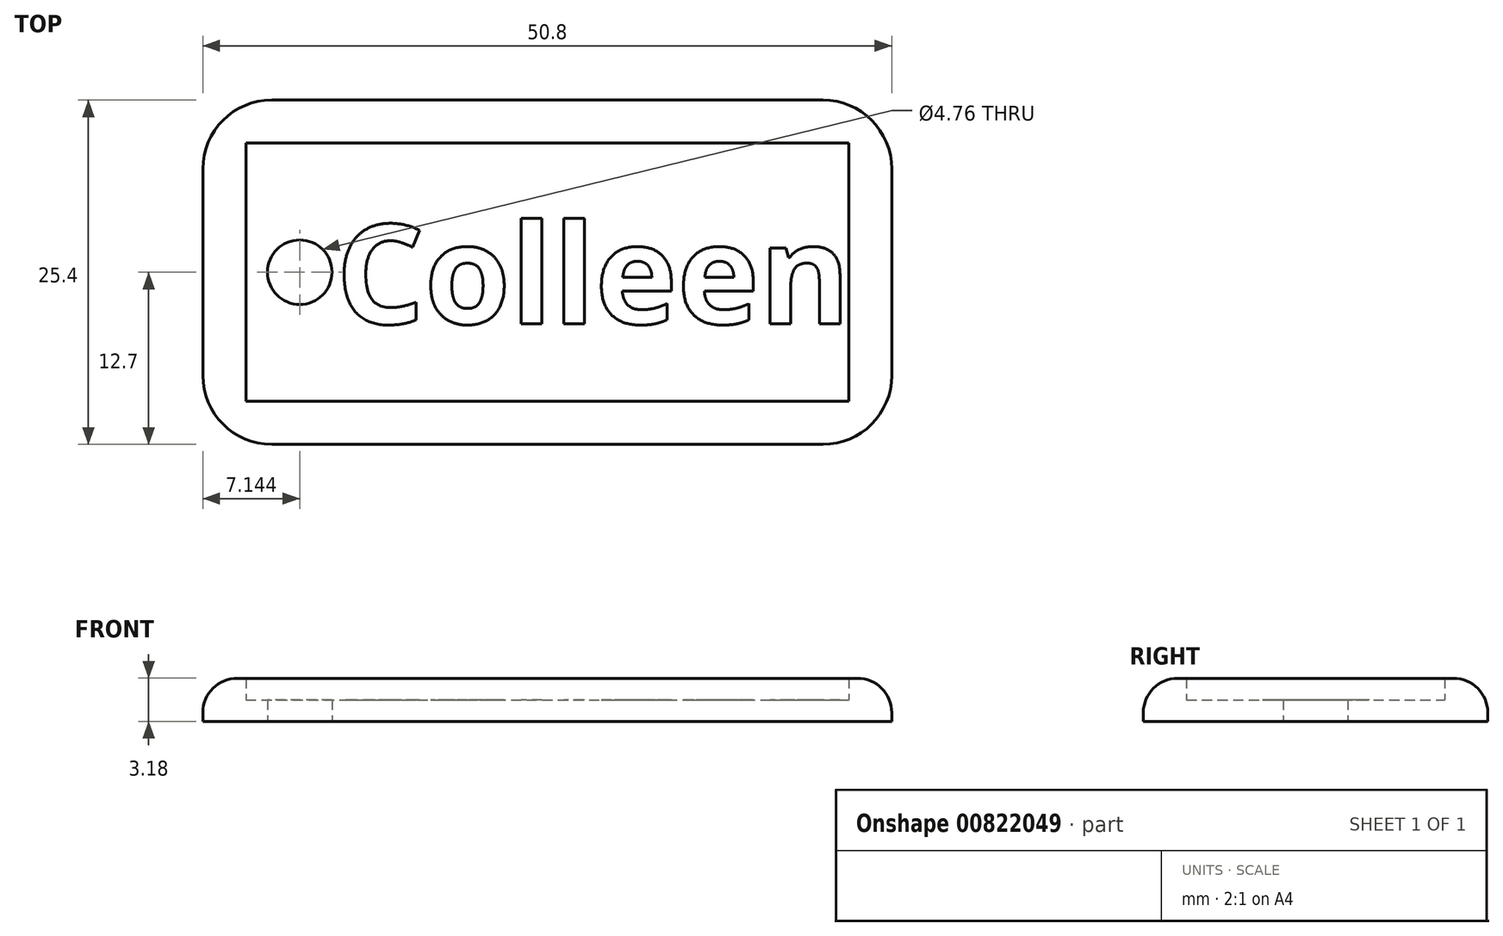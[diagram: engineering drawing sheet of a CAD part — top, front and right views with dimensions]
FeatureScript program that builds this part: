
annotation { "Feature Type Name" : "Feature", "Feature Type Description" : "" }
export const myFeature = defineFeature(function(context is Context, id is Id, definition is map)
    precondition{}
    {
        {
            var Q0;
            Q0=qCreatedBy(makeId("Top.planeOp"),FACE);
            var sketch = newSketch(context, id + "F0", { "sketchPlane" : qUnion([Q0])});
            skLineSegment(sketch, "E0.bottom", {"start": v(0, 0) * mm, "end": v(50.8, 0) * mm});
            skLineSegment(sketch, "E0.top", {"start": v(0, 25.4) * mm, "end": v(50.8, 25.4) * mm});
            skLineSegment(sketch, "E0.left", {"start": v(0, 0) * mm, "end": v(0, 25.4) * mm});
            skLineSegment(sketch, "E0.right", {"start": v(50.8, 0) * mm, "end": v(50.8, 25.4) * mm});
            skCircle(sketch, "E1", {"center": v(7.14, 12.7) * mm, "radius": 2.38 * mm});
            skPoint(sketch, "E1.centerSnap0", {"position": v(0, 12.7) * mm});
            skLineSegment(sketch, "E2.0", {"start": v(3.17, 22.23) * mm, "end": v(47.62, 22.23) * mm});
            skLineSegment(sketch, "E2.1", {"start": v(3.18, 3.18) * mm, "end": v(3.17, 22.22) * mm});
            skLineSegment(sketch, "E2.2", {"start": v(3.18, 3.18) * mm, "end": v(47.62, 3.18) * mm});
            skLineSegment(sketch, "E2.3", {"start": v(47.62, 3.18) * mm, "end": v(47.62, 22.23) * mm});
            skSolve(sketch);
        }
        {
            var Q0;
            Q0=makeQuery(id+"F0.imprint","IMPRINT",FACE,{"disambiguationData":[TD([[makeQuery(id+"F0.imprint","IMPRINT",EDGE,{"derivedFrom":sQuery(id+"F0.wireOp",EDGE,"E1")}),-1.0]])]});
            extrude(context, id + "F1", {"entities" : qUnion([Q0]), "depth" : 1.59 * mm, "offsetDistance" : 25.4 * mm});
        }
        {
            var Q0;
            Q0 = qSketchRegion(id + "F0", true);
            extrude(context, id + "F2", {"entities" : qUnion([Q0]), "operationType" : NewBodyOperationType.ADD, "depth" : 3.17 * mm, "offsetDistance" : 25.4 * mm});
        }
        {
            var Q0;
            Q0=makeQuery(id+"F2.opExtrude","SWEPT_EDGE",EDGE,{"disambiguationData":[OSD([sQuery(id+"F0.wireOp",EDGE,"E0.bottom"),sQuery(id+"F0.wireOp",EDGE,"E0.right")])]});
            var Q1;
            Q1=makeQuery(id+"F2.opExtrude","SWEPT_EDGE",EDGE,{"disambiguationData":[OSD([sQuery(id+"F0.wireOp",EDGE,"E0.top"),sQuery(id+"F0.wireOp",EDGE,"E0.right")])]});
            var Q2;
            Q2=makeQuery(id+"F2.opExtrude","SWEPT_EDGE",EDGE,{"disambiguationData":[OSD([sQuery(id+"F0.wireOp",EDGE,"E0.top"),sQuery(id+"F0.wireOp",EDGE,"E0.left")])]});
            var Q3;
            Q3=makeQuery(id+"F2.opExtrude","SWEPT_EDGE",EDGE,{"disambiguationData":[OSD([sQuery(id+"F0.wireOp",EDGE,"E0.bottom"),sQuery(id+"F0.wireOp",EDGE,"E0.left")])]});
            fillet(context, id + "F3", {"entities" : qUnion([Q0, Q1, Q2, Q3]), "radius" : 5.08 * mm, "tangentPropagation" : true, "allowEdgeOverflow" : false});
        }
        {
            var Q0;
            Q0=makeQuery(id+"F2.opExtrude","CAP_EDGE",EDGE,{"disambiguationData":[OSD([sQuery(id+"F0.wireOp",EDGE,"E0.top")])],"isStart":false});
            var Q1;
            Q1=makeQuery(id+"F2.opExtrude","CAP_EDGE",EDGE,{"disambiguationData":[OSD([sQuery(id+"F0.wireOp",EDGE,"E0.bottom")])],"isStart":false});
            fillet(context, id + "F4", {"entities" : qUnion([Q0, Q1]), "radius" : 2.54 * mm, "tangentPropagation" : true, "allowEdgeOverflow" : false});
        }
        {
            var Q0;
            Q0=makeQuery(id+"F1.opExtrude","CAP_FACE",FACE,{"disambiguationData":[OSD([sQuery(id+"F0.wireOp",EDGE,"E1"),sQuery(id+"F0.wireOp",EDGE,"E2.0"),sQuery(id+"F0.wireOp",EDGE,"E2.1"),sQuery(id+"F0.wireOp",EDGE,"E2.2"),sQuery(id+"F0.wireOp",EDGE,"E2.3")])],"isStart":false});
            var sketch = newSketch(context, id + "F5", { "sketchPlane" : qUnion([Q0])});
            skText(sketch, "E3", { "text": "Colleen", "fontName": "OpenSans-Bold.ttf"});
            const initialGuessF5  = {"E3": [0.00982, 0.0089, 1, 0, 0.00737]};
            skSetInitialGuess(sketch, initialGuessF5);
            skSolve(sketch);
        }
        {
            var Q0;
            Q0=makeQuery(id+"F5.imprint","IMPRINT",FACE,{"disambiguationData":[TD([[makeQuery(id+"F5.imprint","IMPRINT",EDGE,{"derivedFrom":sQuery(id+"F5.wireOp",EDGE,"E3.sketch_text.stroke-0")}),1.0]])]});
            var sketch = newSketch(context, id + "F6", { "sketchPlane" : qUnion([Q0])});
            skSolve(sketch);
        }
        {
            var Q0;
            Q0 = qSketchRegion(id + "F6", true);
            var Q1;
            Q1 = qSketchRegion(id + "F5", true);
            extrude(context, id + "F7", {"entities" : qUnion([Q0, Q1]), "operationType" : NewBodyOperationType.ADD, "depth" : 1 / 812.8 * mm, "offsetDistance" : 25.4 * mm});
        }
    });
